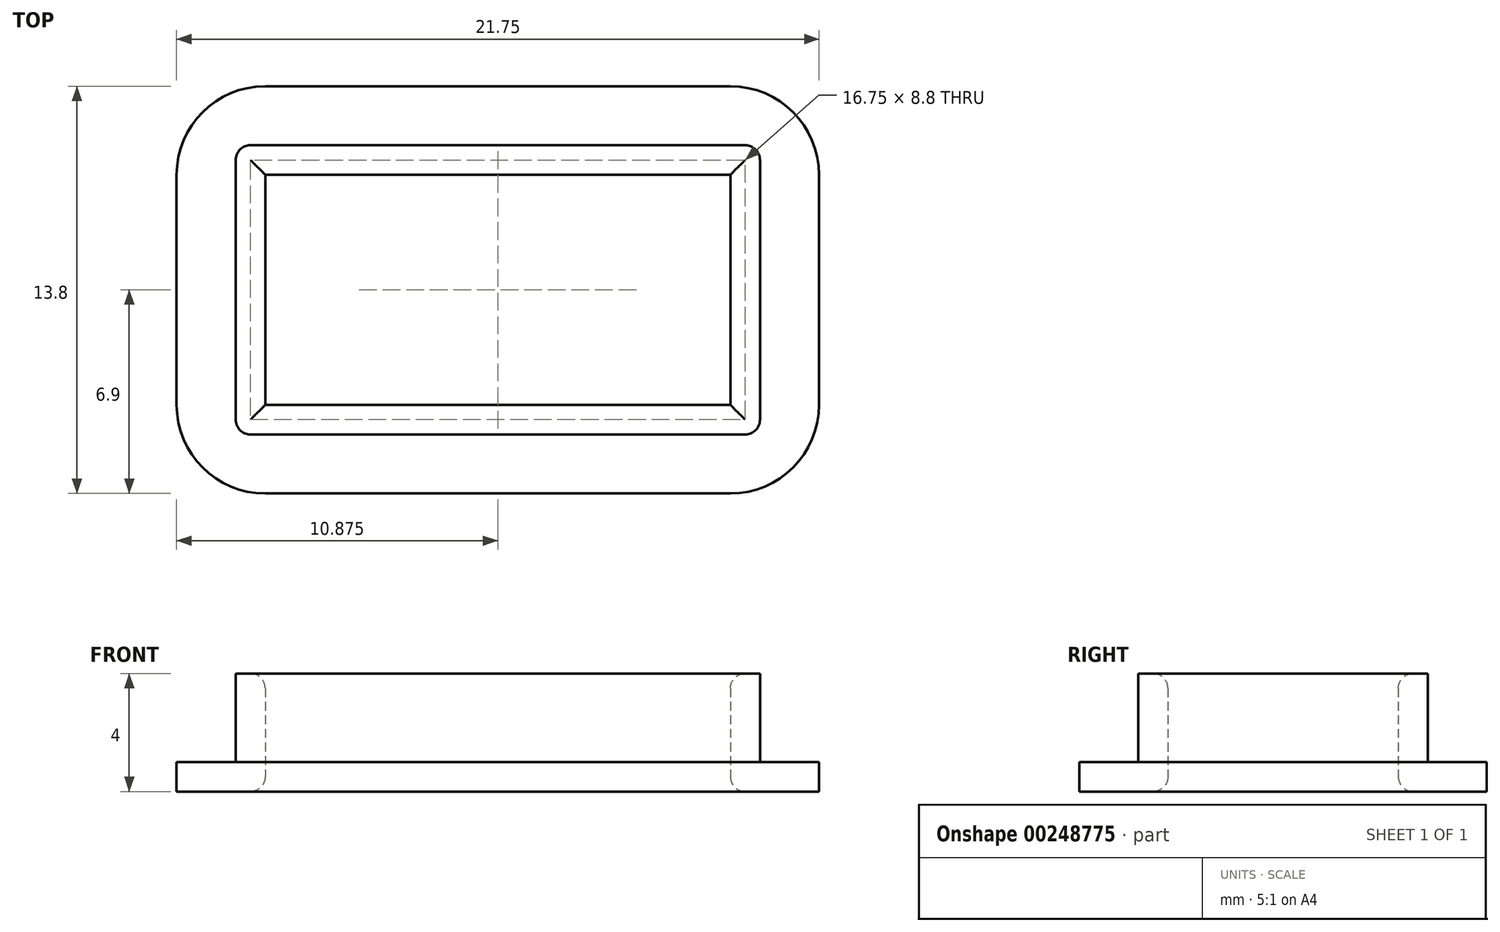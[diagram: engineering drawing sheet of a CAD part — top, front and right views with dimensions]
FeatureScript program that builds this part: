
annotation { "Feature Type Name" : "Feature", "Feature Type Description" : "" }
export const myFeature = defineFeature(function(context is Context, id is Id, definition is map)
    precondition{}
    {
        {
            var Q0;
            Q0=qCreatedBy(makeId("Top.planeOp"),FACE);
            var sketch = newSketch(context, id + "F0", { "sketchPlane" : qUnion([Q0])});
            skLineSegment(sketch, "E0.bottom", {"start": v(0, 0) * mm, "end": v(21.75, 0) * mm});
            skLineSegment(sketch, "E0.top", {"start": v(0, 13.8) * mm, "end": v(21.75, 13.8) * mm});
            skLineSegment(sketch, "E0.left", {"start": v(0, 0) * mm, "end": v(0, 13.8) * mm});
            skLineSegment(sketch, "E0.right", {"start": v(21.75, 0) * mm, "end": v(21.75, 13.8) * mm});
            skLineSegment(sketch, "E1.bottom", {"start": v(2, 2) * mm, "end": v(19.75, 2) * mm});
            skLineSegment(sketch, "E1.top", {"start": v(2, 11.8) * mm, "end": v(19.75, 11.8) * mm});
            skLineSegment(sketch, "E1.left", {"start": v(2, 2) * mm, "end": v(2, 11.8) * mm});
            skLineSegment(sketch, "E1.right", {"start": v(19.75, 2) * mm, "end": v(19.75, 11.8) * mm});
            skLineSegment(sketch, "E2.bottom", {"start": v(3, 10.8) * mm, "end": v(18.75, 10.8) * mm});
            skLineSegment(sketch, "E2.top", {"start": v(3, 3) * mm, "end": v(18.75, 3) * mm});
            skLineSegment(sketch, "E2.left", {"start": v(3, 10.8) * mm, "end": v(3, 3) * mm});
            skLineSegment(sketch, "E2.right", {"start": v(18.75, 10.8) * mm, "end": v(18.75, 3) * mm});
            skSolve(sketch);
        }
        {
            var Q0;
            Q0=makeQuery(id+"F0.imprint","IMPRINT",FACE,{"disambiguationData":[TD([[makeQuery(id+"F0.imprint","IMPRINT",EDGE,{"derivedFrom":sQuery(id+"F0.wireOp",EDGE,"E0.bottom")}),1.0]])]});
            extrude(context, id + "F1", {"entities" : qUnion([Q0]), "depth" : 1 * mm});
        }
        {
            var Q0;
            Q0=makeQuery(id+"F0.imprint","IMPRINT",FACE,{"disambiguationData":[TD([[makeQuery(id+"F0.imprint","IMPRINT",EDGE,{"derivedFrom":sQuery(id+"F0.wireOp",EDGE,"E1.bottom")}),1.0]])]});
            extrude(context, id + "F2", {"entities" : qUnion([Q0]), "operationType" : NewBodyOperationType.ADD, "depth" : 4 * mm});
        }
        {
            var Q0;
            Q0=makeQuery(id+"F2.opExtrude","CAP_EDGE",EDGE,{"disambiguationData":[OSD([sQuery(id+"F0.wireOp",EDGE,"E2.bottom")])],"isStart":false});
            var Q1;
            Q1=makeQuery(id+"F2.opExtrude","CAP_EDGE",EDGE,{"disambiguationData":[OSD([sQuery(id+"F0.wireOp",EDGE,"E2.right")])],"isStart":false});
            var Q2;
            Q2=makeQuery(id+"F2.opExtrude","CAP_EDGE",EDGE,{"disambiguationData":[OSD([sQuery(id+"F0.wireOp",EDGE,"E2.top")])],"isStart":false});
            var Q3;
            Q3=makeQuery(id+"F2.opExtrude","CAP_EDGE",EDGE,{"disambiguationData":[OSD([sQuery(id+"F0.wireOp",EDGE,"E2.left")])],"isStart":false});
            var Q4;
            Q4=makeQuery(id+"F2.opExtrude","CAP_EDGE",EDGE,{"disambiguationData":[OSD([sQuery(id+"F0.wireOp",EDGE,"E2.bottom")])],"isStart":true});
            var Q5;
            Q5=makeQuery(id+"F2.opExtrude","CAP_EDGE",EDGE,{"disambiguationData":[OSD([sQuery(id+"F0.wireOp",EDGE,"E2.left")])],"isStart":true});
            var Q6;
            Q6=makeQuery(id+"F2.opExtrude","CAP_EDGE",EDGE,{"disambiguationData":[OSD([sQuery(id+"F0.wireOp",EDGE,"E2.top")])],"isStart":true});
            var Q7;
            Q7=makeQuery(id+"F2.opExtrude","CAP_EDGE",EDGE,{"disambiguationData":[OSD([sQuery(id+"F0.wireOp",EDGE,"E2.right")])],"isStart":true});
            fillet(context, id + "F3", {"entities" : qUnion([Q0, Q1, Q2, Q3, Q4, Q5, Q6, Q7]), "radius" : .5 * mm, "tangentPropagation" : true, "allowEdgeOverflow" : false});
        }
        {
            var Q0;
            Q0=makeQuery(id+"F2.opExtrude","SWEPT_EDGE",EDGE,{"disambiguationData":[OSD([sQuery(id+"F0.wireOp",EDGE,"E1.top"),sQuery(id+"F0.wireOp",EDGE,"E1.left")])]});
            var Q1;
            Q1=makeQuery(id+"F2.opExtrude","SWEPT_EDGE",EDGE,{"disambiguationData":[OSD([sQuery(id+"F0.wireOp",EDGE,"E1.bottom"),sQuery(id+"F0.wireOp",EDGE,"E1.left")])]});
            var Q2;
            Q2=makeQuery(id+"F2.opExtrude","SWEPT_EDGE",EDGE,{"disambiguationData":[OSD([sQuery(id+"F0.wireOp",EDGE,"E1.bottom"),sQuery(id+"F0.wireOp",EDGE,"E1.right")])]});
            var Q3;
            Q3=makeQuery(id+"F2.opExtrude","SWEPT_EDGE",EDGE,{"disambiguationData":[OSD([sQuery(id+"F0.wireOp",EDGE,"E1.top"),sQuery(id+"F0.wireOp",EDGE,"E1.right")])]});
            fillet(context, id + "F4", {"entities" : qUnion([Q0, Q1, Q2, Q3]), "radius" : .5 * mm, "tangentPropagation" : true, "allowEdgeOverflow" : false});
        }
        {
            var Q0;
            Q0=makeQuery(id+"F1.opExtrude","SWEPT_EDGE",EDGE,{"disambiguationData":[OSD([sQuery(id+"F0.wireOp",EDGE,"E0.top"),sQuery(id+"F0.wireOp",EDGE,"E0.left")])]});
            var Q1;
            Q1=makeQuery(id+"F1.opExtrude","SWEPT_EDGE",EDGE,{"disambiguationData":[OSD([sQuery(id+"F0.wireOp",EDGE,"E0.top"),sQuery(id+"F0.wireOp",EDGE,"E0.right")])]});
            var Q2;
            Q2=makeQuery(id+"F1.opExtrude","SWEPT_EDGE",EDGE,{"disambiguationData":[OSD([sQuery(id+"F0.wireOp",EDGE,"E0.bottom"),sQuery(id+"F0.wireOp",EDGE,"E0.right")])]});
            var Q3;
            Q3=makeQuery(id+"F1.opExtrude","SWEPT_EDGE",EDGE,{"disambiguationData":[OSD([sQuery(id+"F0.wireOp",EDGE,"E0.bottom"),sQuery(id+"F0.wireOp",EDGE,"E0.left")])]});
            fillet(context, id + "F5", {"entities" : qUnion([Q0, Q1, Q2, Q3]), "radius" : 3 * mm, "tangentPropagation" : true, "allowEdgeOverflow" : false});
        }
    });
